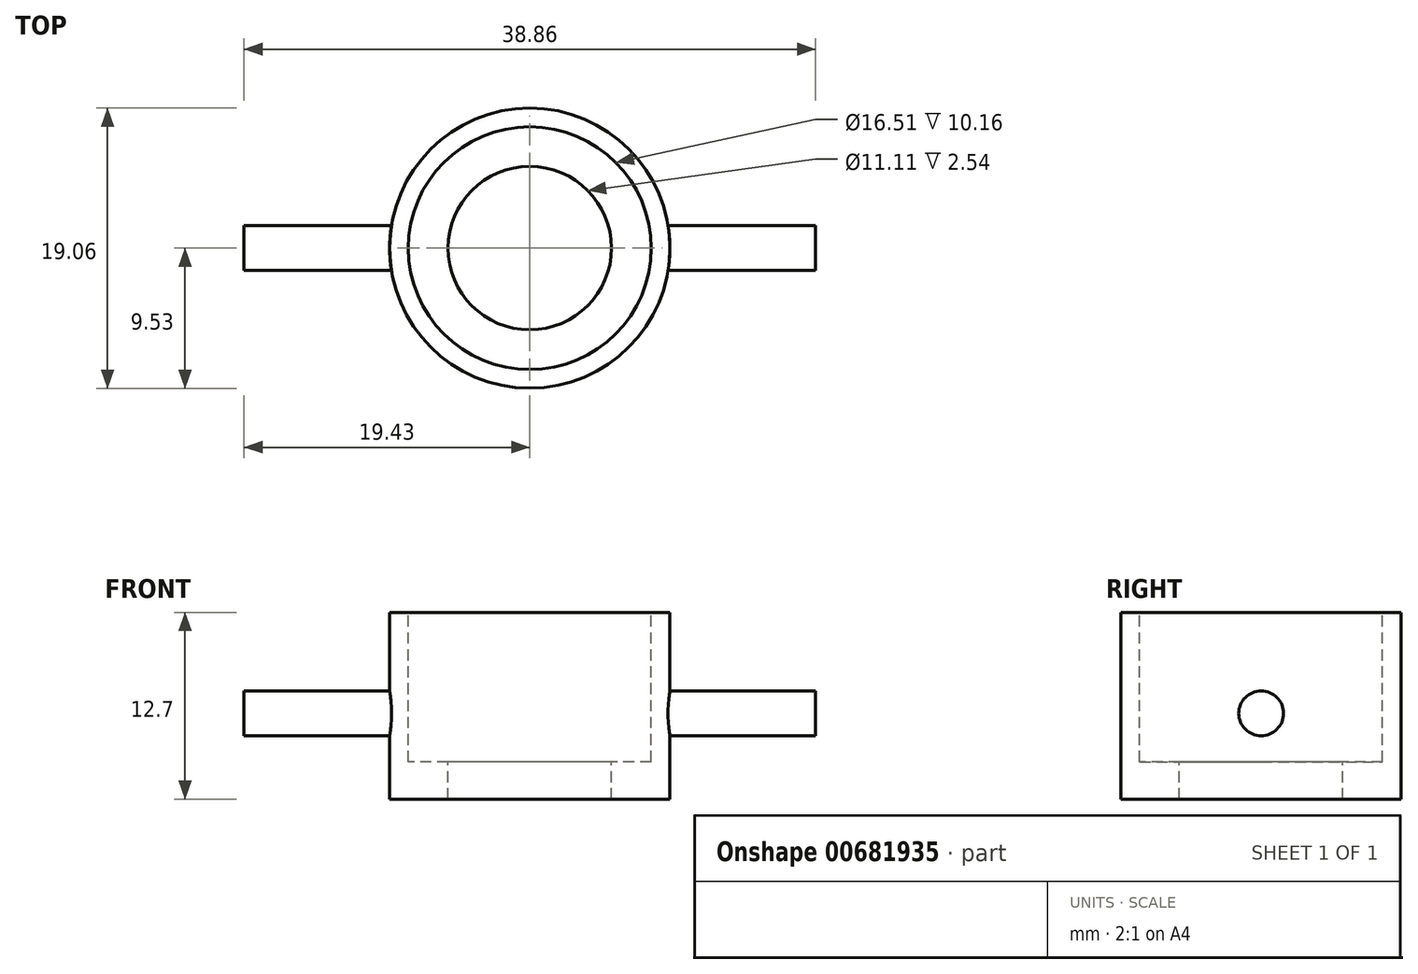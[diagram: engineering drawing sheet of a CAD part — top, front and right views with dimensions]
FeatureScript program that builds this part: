
annotation { "Feature Type Name" : "Feature", "Feature Type Description" : "" }
export const myFeature = defineFeature(function(context is Context, id is Id, definition is map)
    precondition{}
    {
        {
            var Q0;
            Q0=qCreatedBy(makeId("Top.planeOp"),FACE);
            var sketch = newSketch(context, id + "F0", { "sketchPlane" : qUnion([Q0])});
            skCircle(sketch, "E0", {"center": v(0, 0) * mm, "radius": 9.53 * mm});
            skSolve(sketch);
        }
        {
            var Q0;
            Q0=makeQuery(id+"F0.imprint","IMPRINT",FACE,{"disambiguationData":[TD([[makeQuery(id+"F0.imprint","IMPRINT",EDGE,{"derivedFrom":sQuery(id+"F0.wireOp",EDGE,"E0")}),1.0]])]});
            extrude(context, id + "F1", {"entities" : qUnion([Q0]), "depth" : 12.7 * mm, "offsetDistance" : 25.4 * mm});
        }
        {
            var Q0;
            Q0=makeQuery(id+"F1.opExtrude","CAP_FACE",FACE,{"disambiguationData":[OSD([sQuery(id+"F0.wireOp",EDGE,"E0")])],"isStart":false});
            var sketch = newSketch(context, id + "F2", { "sketchPlane" : qUnion([Q0])});
            skCircle(sketch, "E1", {"center": v(0, 0) * mm, "radius": 8.26 * mm});
            skSolve(sketch);
        }
        {
            var Q0;
            Q0 = qSketchRegion(id + "F2", true);
            extrude(context, id + "F3", {"entities" : qUnion([Q0]), "operationType" : NewBodyOperationType.REMOVE, "oppositeDirection" : true, "depth" : 10.16 * mm, "offsetDistance" : 25.4 * mm});
        }
        {
            var Q0;
            Q0=makeQuery(id+"F3.boolean.opBoolean","COPY",FACE,{"derivedFrom":makeQuery(id+"F3.opExtrude","CAP_FACE",FACE,{"disambiguationData":[OSD([sQuery(id+"F2.wireOp",EDGE,"E1")])],"isStart":false})});
            var sketch = newSketch(context, id + "F4", { "sketchPlane" : qUnion([Q0])});
            skCircle(sketch, "E2", {"center": v(0, 0) * mm, "radius": 5.56 * mm});
            skSolve(sketch);
        }
        {
            var Q0;
            Q0 = qSketchRegion(id + "F4", true);
            extrude(context, id + "F5", {"entities" : qUnion([Q0]), "operationType" : NewBodyOperationType.REMOVE, "oppositeDirection" : true, "depth" : 25.4 * mm, "offsetDistance" : 25.4 * mm});
        }
        {
            var Q0;
            Q0=qCreatedBy(makeId("Right.planeOp"),FACE);
            cPlane(context, id + "F6", {"entities" : qUnion([Q0]), "cplaneType" : CPlaneType.OFFSET, "offset" : 9.27 * mm, "width" : 152.4 * mm, "height" : 152.4 * mm});
        }
        {
            var Q0;
            Q0=qCreatedBy(id+"F6.planeOp",FACE);
            var sketch = newSketch(context, id + "F7", { "sketchPlane" : qUnion([Q0])});
            skCircle(sketch, "E3", {"center": v(0, 5.84) * mm, "radius": 1.52 * mm});
            skSolve(sketch);
        }
        {
            var Q0;
            Q0 = qSketchRegion(id + "F7", true);
            extrude(context, id + "F8", {"entities" : qUnion([Q0]), "operationType" : NewBodyOperationType.ADD, "depth" : 10.16 * mm, "offsetDistance" : 25.4 * mm});
        }
        {
            var Q0;
            Q0=makeQuery(id+"F1.opExtrude","SWEPT_BODY",BODY,{"disambiguationData":[OSD([sQuery(id+"F0.wireOp",EDGE,"E0")])]});
            var Q1;
            Q1=qCreatedBy(makeId("Right.planeOp"),FACE);
            mirror(context, id + "F9", {"operationType" : NewBodyOperationType.ADD, "entities" : qUnion([Q0]), "mirrorPlane" : qUnion([Q1])});
        }
    });
